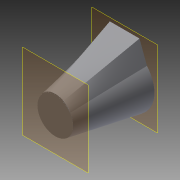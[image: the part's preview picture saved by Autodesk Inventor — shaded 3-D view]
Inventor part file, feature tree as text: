
AUTODESK INVENTOR PART (.ipt)
format: ipt  version: 2015 (Build 190159000, 159)  size: 128,000 bytes
history: native  units: in
note: dims shown in document units (in); Inventor stores cm internally (conversion verified against a paired STEP export)
features: sketch x4, loft x2, plane x1
ambient origin geometry x8: Origin, YZ Plane, XZ Plane, XY Plane, X Axis, Y Axis, Z Axis, Center Point
bodies: Solid1 (feature_tree)
feature tree (7):
  sketch  "Sketch1"  dims[d0=1.75in d1=0.9in]
  plane  "Work Plane1"
  sketch  "Sketch2"  dims[d4=0.42in d5=0.0in d6=90.0deg]
  sketch  "Sketch3"  dims[d7=0.0in d8=90.0deg]
  sketch  "Sketch4"  dims[d9=0.45in d10=0.0in d11=90.0deg d12=0.0in d13=90.0deg]
  loft  "Loft1"
  loft  "Loft2"
